# Revit family: PRD_FrankeWS_WtrSpplFttngsFrWshBsnsAndTrghs_SelfClosingTapMixer_F5ST1004-1006
name_source: partatom
category: Plumbing Fixtures
revit_build: Autodesk Revit 2018 (Build: 20190510_1515(x64)
units: mm (PartAtom-declared; Revit-internal decimal feet)

## family parameters
Cut with Voids When Loaded = No
Host = Face
OmniClass Number = 23.45.55.17
OmniClass Title = Mixing Faucets
Part Type = Normal
Room Calculation Point = No
Round Connector Dimension = Use Diameter
Shared = No

## types (3) — shared parameters
AdjustableFlowTime = yes
AssetType = Fixed
Category = Pr_40_20_87_98, Washbasin taps
Color = Chrome
Default Elevation = 850 mm  [stored 2.78871 ft]
DefaultAutomaticHygieneFlushing = fixed interval 24 hours
Depressurised = no
DiameterNominal = 15.000 mm
DurationUnit = year
FaucetFunction = MIXED
FaucetOperation = SELFCLOSING
FaucetType = BIB
Features = For sanitary facilities. Connects to hot water and cold water. High-polished chromium-plated brass.
Finish = high-polished chromium-plated brass
FlowColdWater = 0.1 L/s
FlowHotWater = 0.1 L/s
FunctionalPrinciple = hydraulic self-closing
HygieneFlushing = yes
IfcExportAs = IfcValveType
IfcExportType = FAUCET
InletSize = G-1-2-B
Manufacturer = KWC Group AG
ManufacturerName = KWC Group AG
ManufacturerURL = www.kwc.com
Material = Brass
MaterialsBody = Brass
MaximumFlowTime = 35.00 seconds
MinimumFlowPressure = 1.00 bar
MinimumFlowTime = 5.00 seconds
NBSDescription = Water supply fittings for wash basins and troughs
NBSReference = 45-35-70/371
NominalWidth = 317 mm  [stored 1.04003 ft]
OutletMaterial = PRD_AR_SyntheticGrey
PowerConsumption = 1.5
PowerSupplyConnection = Battery 6 V
ProductInformation = https://pim.kwc.com
ProtectiveShutdown = no
ProtectiveSystemIP = IP59K
SensorMaterial = PRD_AR_SyntheticDarkGrey
SoundInsulation = no
TapBottomOffset = 75 mm
TapMaterial = PRD_AR_ChromatedBrass_HighPolished
ThermalDisinfection = manual thermal disinfection
TypeOfMixing = with thermostat
TypeOfMounting = Wall mounting
TypeOfOperation = manual operation
TypeOfSensor = opto-electronic sensor
TypeOfTap = bib tap
URL = www.kwc.com
Uniclass2015Code = Pr_40_20_87_98
Uniclass2015Title = Washbasin taps
Uniclass2015Version = Products v1.10
Version = 1
VolumeFlowRate = 0.10 L/s at 3 bar
WarrantyDurationUnit = year
zero-valued in all types: NominalHeight, NominalLength

## per-type parameters (varying)
| type | BIMObjectName | Description | GrossWeight | LengthToSpout | Model | ModelNumber | ModelReference | Name | NetWeight | SpoutProjection |
| F5ST1004 - 0.1 L/s, projection 135 mm | PRD_AR_WaterSupplyFittingsForWashBasinsAndTroughs_SelfClosingTapMixer_F5ST1004 | F5S-Therm self-closing thermostat wall mixer DN 15 for wall mounting with lockable swivelling spout, for sanitary facilities. Hydraulically controlled, connects to hot water and cold water. With a pre-assembled hygiene unit including sensor with control electronics and 6 V lithium battery (CR-P2) for automatic hygiene flushing and storage of statistical data. FRAMIC self-closing cartridge, hydraulically controlled, low-maintenance and stagnation-free, with ceramic disc technology, self-closing, flow pressure-independent due to medium-separated design. Stepless adjustment of flow duration. Thermostat with metal handle with adjustable and turn-proof temperature stop, with option for performance of manual thermal disinfection. Scald-protected, safe-touch housing, all-metal construction, high-polished chromium-plated brass. Laminar jet controller with integrated flow regulator 6.0 l/min. With adjustable and lockable connections with backflow preventer and strainers, completely covered with depth-adjustable screw rosettes. Projection 135 mm. Activated hygiene flushing, fixed interval of 24 hours. With option for parameterization and communication via optional, bidirectional remote control. | 4.90 kg | 135 mm  [stored 0.442913 ft] | F5ST1004 | 2030040242 | F5ST1004 | F5 self-closing tap mixer F5ST1004 | 4.70 kg | 135.00 mm |
| F5ST1005 - 0.1 L/s, projection 195 mm | PRD_AR_WaterSupplyFittingsForWashBasinsAndTroughs_SelfClosingTapMixer_F5ST1005 | F5S-Therm self-closing thermostat wall mixer DN 15 for wall mounting with lockable swivelling spout, for sanitary facilities. Hydraulically controlled, connects to hot water and cold water. With a pre-assembled hygiene unit including sensor with control electronics and 6 V lithium battery (CR-P2) for automatic hygiene flushing and storage of statistical data. FRAMIC self-closing cartridge, hydraulically controlled, low-maintenance and stagnation-free, with ceramic disc technology, self-closing, flow pressure-independent due to medium-separated design. Stepless adjustment of flow duration. Thermostat with metal handle with adjustable and turn-proof temperature stop, with option for performance of manual thermal disinfection. Scald-protected, safe-touch housing, all-metal construction, high-polished chromium-plated brass. Laminar jet controller with integrated flow regulator 6.0 l/min. With adjustable and lockable connections with backflow preventer and strainers, completely covered with depth-adjustable screw rosettes. Projection 195 mm. Activated hygiene flushing, fixed interval of 24 hours. With option for parameterization and communication via optional, bidirectional remote control. | 5.00 kg | 195 mm  [stored 0.639764 ft] | F5ST1005 | 2030040243 | F5ST1005 | F5 self-closing tap mixer F5ST1005 | 4.80 kg | 195.00 mm |
| F5ST1006 - 0.1 L/s, projection 255 mm | PRD_AR_WaterSupplyFittingsForWashBasinsAndTroughs_SelfClosingTapMixer_F5ST1006 | F5S-Therm self-closing thermostat wall mixer DN 15 for wall mounting with lockable swivelling spout, for sanitary facilities. Hydraulically controlled, connects to hot water and cold water. With a pre-assembled hygiene unit including sensor with control electronics and 6 V lithium battery (CR-P2) for automatic hygiene flushing and storage of statistical data. FRAMIC self-closing cartridge, hydraulically controlled, low-maintenance and stagnation-free, with ceramic disc technology, self-closing, flow pressure-independent due to medium-separated design. Stepless adjustment of flow duration. Thermostat with metal handle with adjustable and turn-proof temperature stop, with option for performance of manual thermal disinfection. Scald-protected, safe-touch housing, all-metal construction, high-polished chromium-plated brass. Laminar jet controller with integrated flow regulator 6.0 l/min. With adjustable and lockable connections with backflow preventer and strainers, completely covered with depth-adjustable screw rosettes. Projection 255 mm. Activated hygiene flushing, fixed interval of 24 hours. With option for parameterization and communication via optional, bidirectional remote control. | 5.10 kg | 255 mm  [stored 0.836614 ft] | F5ST1006 | 2030040288 | F5ST1006 | F5 self-closing tap mixer F5ST1006 | 5.00 kg | 255.00 mm |

note: [stored X ft] marks values corroborated as IEEE doubles in the binary element streams (Revit-internal decimal feet)

## geometry (parser evidence)
native form markers: Sweep x5
no freeform markers — native parametric forms only
